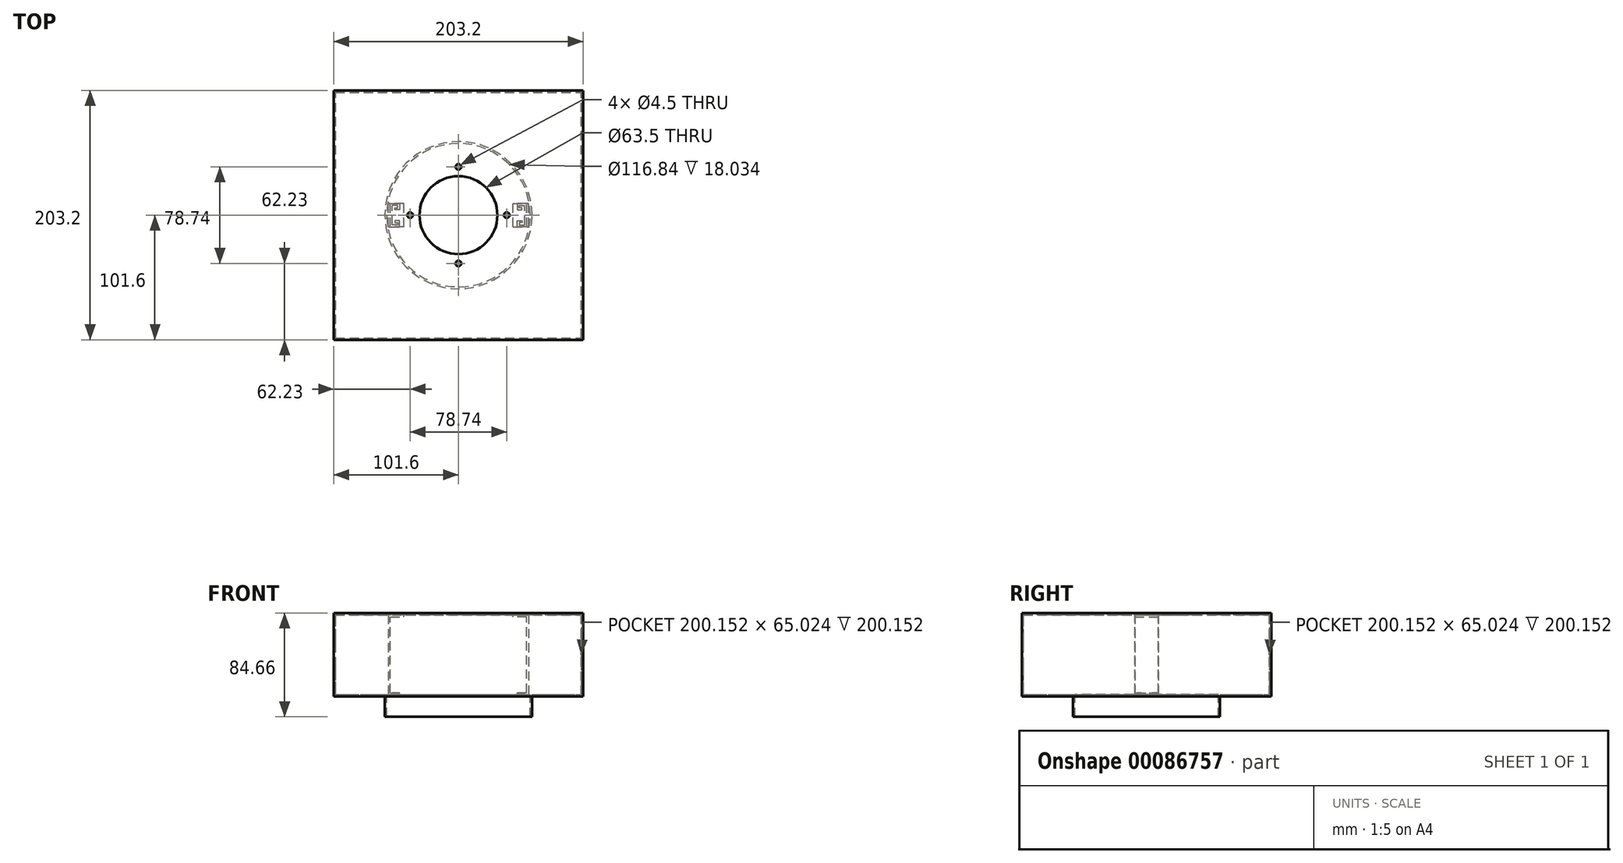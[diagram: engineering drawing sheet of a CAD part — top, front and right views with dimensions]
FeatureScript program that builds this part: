
annotation { "Feature Type Name" : "Feature", "Feature Type Description" : "" }
export const myFeature = defineFeature(function(context is Context, id is Id, definition is map)
    precondition{}
    {
        {
            var Q0;
            Q0=qCreatedBy(makeId("Top.planeOp"),FACE);
            var sketch = newSketch(context, id + "F0", { "sketchPlane" : qUnion([Q0])});
            skLineSegment(sketch, "E0.bottom", {"start": v(-101.6, 101.6) * mm, "end": v(101.6, 101.6) * mm});
            skLineSegment(sketch, "E0.top", {"start": v(-101.6, -101.6) * mm, "end": v(101.6, -101.6) * mm});
            skLineSegment(sketch, "E0.left", {"start": v(-101.6, 101.6) * mm, "end": v(-101.6, -101.6) * mm});
            skLineSegment(sketch, "E0.right", {"start": v(101.6, 101.6) * mm, "end": v(101.6, -101.6) * mm});
            skPoint(sketch, "E0.middle", {"position": v(0, 0) * mm});
            skSolve(sketch);
        }
        {
            var Q0;
            Q0 = qSketchRegion(id + "F0", true);
            extrude(context, id + "F1", {"entities" : qUnion([Q0]), "oppositeDirection" : true, "depth" : 1.6 * mm});
        }
        {
            var Q0;
            Q0=makeQuery(id+"F1.opExtrude","CAP_FACE",FACE,{"disambiguationData":[OSD([sQuery(id+"F0.wireOp",EDGE,"E0.bottom"),sQuery(id+"F0.wireOp",EDGE,"E0.top"),sQuery(id+"F0.wireOp",EDGE,"E0.left"),sQuery(id+"F0.wireOp",EDGE,"E0.right")])],"isStart":true});
            var sketch = newSketch(context, id + "F2", { "sketchPlane" : qUnion([Q0])});
            skCircle(sketch, "E1", {"center": v(0, 0) * mm, "radius": 31.75 * mm});
            skCircle(sketch, "E2", {"center": v(0, 39.37) * mm, "radius": 2.25 * mm});
            skCircle(sketch, "E3.1.0", {"center": v(-39.37, 0) * mm, "radius": 2.25 * mm});
            skCircle(sketch, "E3.2.0", {"center": v(0, -39.37) * mm, "radius": 2.25 * mm});
            skCircle(sketch, "E3.3.0", {"center": v(39.37, 0) * mm, "radius": 2.25 * mm});
            skSolve(sketch);
        }
        {
            var Q0;
            Q0 = qSketchRegion(id + "F2", true);
            extrude(context, id + "F3", {"entities" : qUnion([Q0]), "operationType" : NewBodyOperationType.REMOVE, "endBound" : BoundingType.UP_TO_NEXT, "oppositeDirection" : true, "depth" : 25.4 * mm});
        }
        {
            var Q0;
            Q0=qCreatedBy(makeId("Front.planeOp"),FACE);
            var sketch = newSketch(context, id + "F4", { "sketchPlane" : qUnion([Q0])});
            skLineSegment(sketch, "E4.0", {"start": v(31.75, -1.6) * mm, "end": v(-31.75, -1.6) * mm, "construction": true});
            skLineSegment(sketch, "E5", {"start": v(0, 0) * mm, "end": v(0, -124.12) * mm, "construction": true});
            skLineSegment(sketch, "E6.MirrorCS", {"start": v(-31.75, -1.6) * mm, "end": v(31.75, -1.6) * mm, "construction": true});
            skLineSegment(sketch, "E7", {"start": v(44.45, -1.6) * mm, "end": v(57.15, -1.6) * mm});
            skLineSegment(sketch, "E8", {"start": v(57.15, -1.6) * mm, "end": v(57.15, -65.1) * mm});
            skLineSegment(sketch, "E9", {"start": v(57.15, -65.1) * mm, "end": v(55.55, -65.1) * mm});
            skLineSegment(sketch, "E10", {"start": v(55.55, -65.1) * mm, "end": v(55.55, -3.2) * mm});
            skLineSegment(sketch, "E11", {"start": v(55.55, -3.2) * mm, "end": v(44.45, -3.2) * mm});
            skLineSegment(sketch, "E12", {"start": v(44.45, -3.2) * mm, "end": v(44.45, -1.6) * mm});
            skLineSegment(sketch, "E13.MirrorCS", {"start": v(-57.15, -65.1) * mm, "end": v(-55.55, -65.1) * mm});
            skLineSegment(sketch, "E14.MirrorCS", {"start": v(-44.45, -3.2) * mm, "end": v(-44.45, -1.6) * mm});
            skLineSegment(sketch, "E15.MirrorCS", {"start": v(-57.15, -1.6) * mm, "end": v(-57.15, -65.1) * mm});
            skLineSegment(sketch, "E16.MirrorCS", {"start": v(-44.45, -1.6) * mm, "end": v(-57.15, -1.6) * mm});
            skLineSegment(sketch, "E17.MirrorCS", {"start": v(-55.55, -3.2) * mm, "end": v(-44.45, -3.2) * mm});
            skLineSegment(sketch, "E18.MirrorCS", {"start": v(-55.55, -65.1) * mm, "end": v(-55.55, -3.2) * mm});
            skSolve(sketch);
        }
        {
            var Q0;
            Q0 = qSketchRegion(id + "F4", true);
            extrude(context, id + "F5", {"entities" : qUnion([Q0]), "operationType" : NewBodyOperationType.ADD, "depth" : 19.05 * mm, "symmetric" : true});
        }
        {
            var Q0;
            Q0=makeQuery(id+"F5.opExtrude","SWEPT_FACE",FACE,{"disambiguationData":[OSD([sQuery(id+"F4.wireOp",EDGE,"E9")])]});
            var sketch = newSketch(context, id + "F6", { "sketchPlane" : qUnion([Q0])});
            skLineSegment(sketch, "E19", {"start": v(55.55, 0) * mm, "end": v(53.96, 0) * mm, "construction": true});
            skPoint(sketch, "E19.endSnap0", {"position": v(55.55, 0) * mm});
            skLineSegment(sketch, "E20", {"start": v(57.15, -9.53) * mm, "end": v(47.93, -9.53) * mm});
            skLineSegment(sketch, "E21", {"start": v(47.93, -9.53) * mm, "end": v(47.93, -4.44) * mm});
            skLineSegment(sketch, "E22", {"start": v(47.93, -4.44) * mm, "end": v(51.74, -4.44) * mm});
            skLineSegment(sketch, "E23", {"start": v(51.74, -4.44) * mm, "end": v(51.74, -6.05) * mm});
            skLineSegment(sketch, "E24", {"start": v(51.74, -6.05) * mm, "end": v(49.53, -6.05) * mm});
            skLineSegment(sketch, "E25", {"start": v(49.53, -6.05) * mm, "end": v(49.53, -7.92) * mm});
            skLineSegment(sketch, "E26", {"start": v(49.53, -7.92) * mm, "end": v(53.95, -7.92) * mm});
            skLineSegment(sketch, "E27", {"start": v(53.95, -7.92) * mm, "end": v(53.95, 0) * mm});
            skLineSegment(sketch, "E28.MirrorCS", {"start": v(49.53, 7.92) * mm, "end": v(53.95, 7.92) * mm});
            skLineSegment(sketch, "E29.MirrorCS", {"start": v(53.95, 7.92) * mm, "end": v(53.95, 0) * mm});
            skLineSegment(sketch, "E30.MirrorCS", {"start": v(49.53, 6.05) * mm, "end": v(49.53, 7.92) * mm});
            skLineSegment(sketch, "E31.MirrorCS", {"start": v(51.74, 6.05) * mm, "end": v(49.53, 6.05) * mm});
            skLineSegment(sketch, "E32.MirrorCS", {"start": v(47.93, 9.52) * mm, "end": v(47.93, 4.44) * mm});
            skLineSegment(sketch, "E33.MirrorCS", {"start": v(51.74, 4.44) * mm, "end": v(51.74, 6.05) * mm});
            skLineSegment(sketch, "E34.MirrorCS", {"start": v(57.15, 9.53) * mm, "end": v(47.93, 9.53) * mm});
            skLineSegment(sketch, "E35.MirrorCS", {"start": v(47.93, 4.45) * mm, "end": v(51.74, 4.45) * mm});
            skLineSegment(sketch, "E36", {"start": v(57.15, -9.53) * mm, "end": v(57.15, 9.53) * mm});
            skPoint(sketch, "E37.orphan", {"position": v(55.55, 9.53) * mm});
            skPoint(sketch, "E38.orphan", {"position": v(55.55, -9.53) * mm});
            skSolve(sketch);
        }
        {
            var Q0;
            Q0 = qSketchRegion(id + "F6", true);
            extrude(context, id + "F7", {"entities" : qUnion([Q0]), "depth" : 1.6 * mm});
        }
        {
            var Q0;
            Q0=makeQuery(id+"F7.opExtrude","SWEPT_BODY",BODY,{"disambiguationData":[OSD([sQuery(id+"F6.wireOp",EDGE,"mPUitfUB-v5yS-3Hze-CKhs-U029XzvzVBiZ"),sQuery(id+"F6.wireOp",EDGE,"E20"),sQuery(id+"F6.wireOp",EDGE,"E21"),sQuery(id+"F6.wireOp",EDGE,"E22"),sQuery(id+"F6.wireOp",EDGE,"E23"),sQuery(id+"F6.wireOp",EDGE,"E24"),sQuery(id+"F6.wireOp",EDGE,"E25"),sQuery(id+"F6.wireOp",EDGE,"E26"),sQuery(id+"F6.wireOp",EDGE,"E27"),sQuery(id+"F6.wireOp",EDGE,"E28.MirrorCS"),sQuery(id+"F6.wireOp",EDGE,"E29.MirrorCS"),sQuery(id+"F6.wireOp",EDGE,"E30.MirrorCS"),sQuery(id+"F6.wireOp",EDGE,"E31.MirrorCS"),sQuery(id+"F6.wireOp",EDGE,"E32.MirrorCS"),sQuery(id+"F6.wireOp",EDGE,"E33.MirrorCS"),sQuery(id+"F6.wireOp",EDGE,"E34.MirrorCS"),sQuery(id+"F6.wireOp",EDGE,"62dfd6e3-fca8-4893-8dfe-90fc95ece2037.MirrorCS"),sQuery(id+"F6.wireOp",EDGE,"E35.MirrorCS")])]});
            var Q1;
            Q1=qCreatedBy(makeId("Right.planeOp"),FACE);
            mirror(context, id + "F8", {"operationType" : NewBodyOperationType.ADD, "entities" : qUnion([Q0]), "mirrorPlane" : qUnion([Q1])});
        }
        {
            var Q0;
            Q0=makeQuery(id+"F1.opExtrude","CAP_FACE",FACE,{"disambiguationData":[OSD([sQuery(id+"F0.wireOp",EDGE,"E0.bottom"),sQuery(id+"F0.wireOp",EDGE,"E0.top"),sQuery(id+"F0.wireOp",EDGE,"E0.left"),sQuery(id+"F0.wireOp",EDGE,"E0.right")])],"isStart":false});
            var sketch = newSketch(context, id + "F9", { "sketchPlane" : qUnion([Q0])});
            skLineSegment(sketch, "E39.bottom", {"start": v(-101.6, 101.6) * mm, "end": v(101.6, 101.6) * mm});
            skLineSegment(sketch, "E39.top", {"start": v(-101.6, -101.6) * mm, "end": v(101.6, -101.6) * mm});
            skLineSegment(sketch, "E39.left", {"start": v(-101.6, 101.6) * mm, "end": v(-101.6, -101.6) * mm});
            skLineSegment(sketch, "E39.right", {"start": v(101.6, 101.6) * mm, "end": v(101.6, -101.6) * mm});
            skLineSegment(sketch, "E40.bottom", {"start": v(-100.08, 100.08) * mm, "end": v(100.08, 100.08) * mm});
            skLineSegment(sketch, "E40.top", {"start": v(-100.08, -100.08) * mm, "end": v(100.08, -100.08) * mm});
            skLineSegment(sketch, "E40.left", {"start": v(-100.08, 100.08) * mm, "end": v(-100.08, -100.08) * mm});
            skLineSegment(sketch, "E40.right", {"start": v(100.08, 100.08) * mm, "end": v(100.08, -100.08) * mm});
            skPoint(sketch, "E40.middle", {"position": v(0, 0) * mm});
            skSolve(sketch);
        }
        {
            var Q0;
            Q0 = qSketchRegion(id + "F9", true);
            extrude(context, id + "F10", {"entities" : qUnion([Q0]), "operationType" : NewBodyOperationType.ADD, "depth" : 65.02 * mm});
        }
        {
            var Q0;
            Q0=makeQuery(id+"F10.opExtrude","CAP_FACE",FACE,{"disambiguationData":[OSD([sQuery(id+"F9.wireOp",EDGE,"E39.bottom"),sQuery(id+"F9.wireOp",EDGE,"E39.top"),sQuery(id+"F9.wireOp",EDGE,"E39.left"),sQuery(id+"F9.wireOp",EDGE,"E39.right"),sQuery(id+"F9.wireOp",EDGE,"E40.bottom"),sQuery(id+"F9.wireOp",EDGE,"E40.top"),sQuery(id+"F9.wireOp",EDGE,"E40.left"),sQuery(id+"F9.wireOp",EDGE,"E40.right")])],"isStart":false});
            var sketch = newSketch(context, id + "F11", { "sketchPlane" : qUnion([Q0])});
            skLineSegment(sketch, "E41.bottom", {"start": v(-101.6, 101.6) * mm, "end": v(101.6, 101.6) * mm});
            skLineSegment(sketch, "E41.top", {"start": v(-101.6, -101.6) * mm, "end": v(101.6, -101.6) * mm});
            skLineSegment(sketch, "E41.left", {"start": v(-101.6, 101.6) * mm, "end": v(-101.6, -101.6) * mm});
            skLineSegment(sketch, "E41.right", {"start": v(101.6, 101.6) * mm, "end": v(101.6, -101.6) * mm});
            skCircle(sketch, "E42", {"center": v(0, 0) * mm, "radius": 58.42 * mm});
            skSolve(sketch);
        }
        {
            var Q0;
            Q0 = qSketchRegion(id + "F11", true);
            extrude(context, id + "F12", {"entities" : qUnion([Q0]), "operationType" : NewBodyOperationType.ADD, "depth" : 1.52 * mm});
        }
        {
            var Q0;
            Q0=makeQuery(id+"F12.opExtrude","CAP_FACE",FACE,{"disambiguationData":[OSD([sQuery(id+"F11.wireOp",EDGE,"E41.bottom"),sQuery(id+"F11.wireOp",EDGE,"E41.top"),sQuery(id+"F11.wireOp",EDGE,"E41.left"),sQuery(id+"F11.wireOp",EDGE,"E41.right"),sQuery(id+"F11.wireOp",EDGE,"E42")])],"isStart":false});
            var sketch = newSketch(context, id + "F13", { "sketchPlane" : qUnion([Q0])});
            skCircle(sketch, "E43.0", {"center": v(0, 0) * mm, "radius": 58.42 * mm});
            skCircle(sketch, "E44", {"center": v(0, 0) * mm, "radius": 59.94 * mm});
            skSolve(sketch);
        }
        {
            var Q0;
            Q0 = qSketchRegion(id + "F13", true);
            extrude(context, id + "F14", {"entities" : qUnion([Q0]), "operationType" : NewBodyOperationType.ADD, "depth" : 16.5 * mm});
        }
    });
